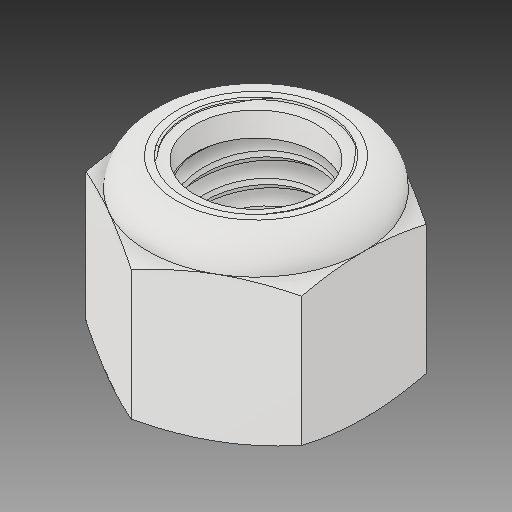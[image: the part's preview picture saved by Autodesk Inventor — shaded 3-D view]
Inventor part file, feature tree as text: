
AUTODESK INVENTOR PART (.ipt)
format: ipt  version: 2019 (Build 230136000, 136)  size: 336,896 bytes
history: native  units: in
note: dims shown in document units (in); Inventor stores cm internally (conversion verified against a paired STEP export)
features: other x1, revolve x1
ambient origin geometry x8: Origin, YZ Plane, XZ Plane, XY Plane, X Axis, Y Axis, Z Axis, Center Point
bodies: Solid1 (feature_tree), Solid2 (feature_tree)
feature tree (2):
  other  "Cut-Revolve4"
  revolve  "Revolve2"  [1 undecoded]
note: 1 required parameter value undecoded (feature->parameter linkage not recoverable at this tier; creation-order binding heuristic only, values carry confidence <= 0.55)
